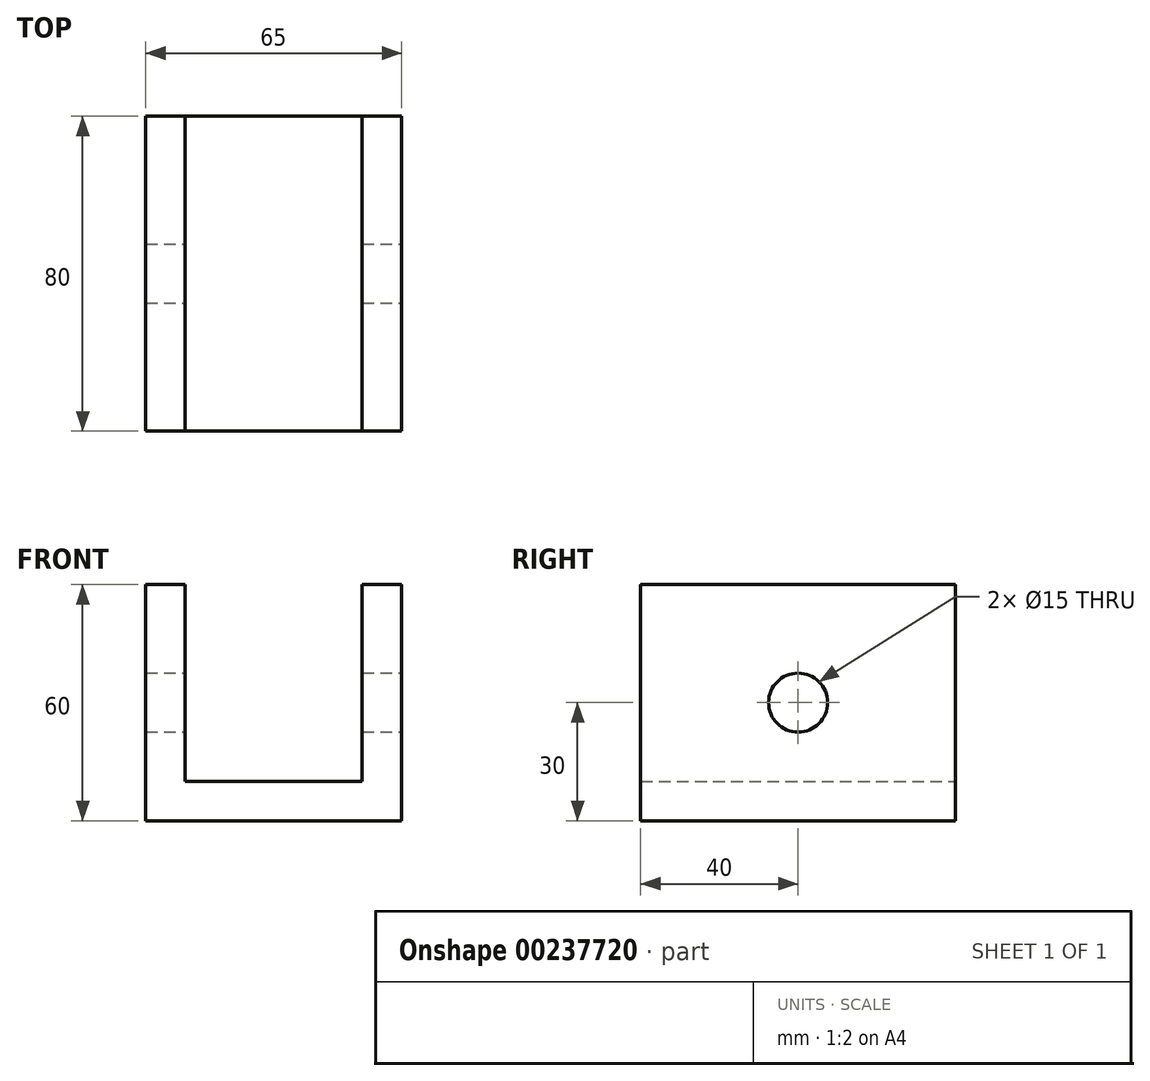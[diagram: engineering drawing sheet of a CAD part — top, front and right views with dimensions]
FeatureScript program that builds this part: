
annotation { "Feature Type Name" : "Feature", "Feature Type Description" : "" }
export const myFeature = defineFeature(function(context is Context, id is Id, definition is map)
    precondition{}
    {
        {
            var Q0;
            Q0=qCreatedBy(makeId("Front.planeOp"),FACE);
            var sketch = newSketch(context, id + "F0", { "sketchPlane" : qUnion([Q0])});
            skLineSegment(sketch, "E0.bottom", {"start": v(-32.5, 60) * mm, "end": v(-22.5, 60) * mm});
            skLineSegment(sketch, "E0.top", {"start": v(-32.5, 0) * mm, "end": v(32.5, 0) * mm});
            skLineSegment(sketch, "E0.left", {"start": v(-32.5, 60) * mm, "end": v(-32.5, 0) * mm});
            skLineSegment(sketch, "E0.right", {"start": v(32.5, 60) * mm, "end": v(32.5, 0) * mm});
            skLineSegment(sketch, "E1", {"start": v(-22.5, 60) * mm, "end": v(-22.5, 10) * mm});
            skLineSegment(sketch, "E2", {"start": v(-22.5, 10) * mm, "end": v(22.5, 10) * mm});
            skLineSegment(sketch, "E3", {"start": v(22.5, 10) * mm, "end": v(22.5, 60) * mm});
            skLineSegment(sketch, "E4.trimOffspring", {"start": v(22.5, 60) * mm, "end": v(32.5, 60) * mm});
            skSolve(sketch);
        }
        {
            var Q0;
            Q0=makeQuery(id+"F0.imprint","IMPRINT",FACE,{"disambiguationData":[TD([[makeQuery(id+"F0.imprint","IMPRINT",EDGE,{"derivedFrom":sQuery(id+"F0.wireOp",EDGE,"E0.bottom")}),-1.0]])]});
            extrude(context, id + "F1", {"entities" : qUnion([Q0]), "endBound" : BoundingType.SYMMETRIC, "depth" : 80 * mm});
        }
        {
            var Q0;
            Q0=qCreatedBy(makeId("Right.planeOp"),FACE);
            var sketch = newSketch(context, id + "F2", { "sketchPlane" : qUnion([Q0])});
            skCircle(sketch, "E5", {"center": v(0, 30) * mm, "radius": 7.5 * mm});
            skSolve(sketch);
        }
        {
            var Q0;
            Q0=makeQuery(id+"F2.imprint","IMPRINT",FACE,{"disambiguationData":[TD([[makeQuery(id+"F2.imprint","IMPRINT",EDGE,{"derivedFrom":sQuery(id+"F2.wireOp",EDGE,"E5")}),1.0]])]});
            extrude(context, id + "F3", {"entities" : qUnion([Q0]), "operationType" : NewBodyOperationType.REMOVE, "endBound" : BoundingType.SYMMETRIC, "oppositeDirection" : true, "depth" : 100 * mm});
        }
    });
